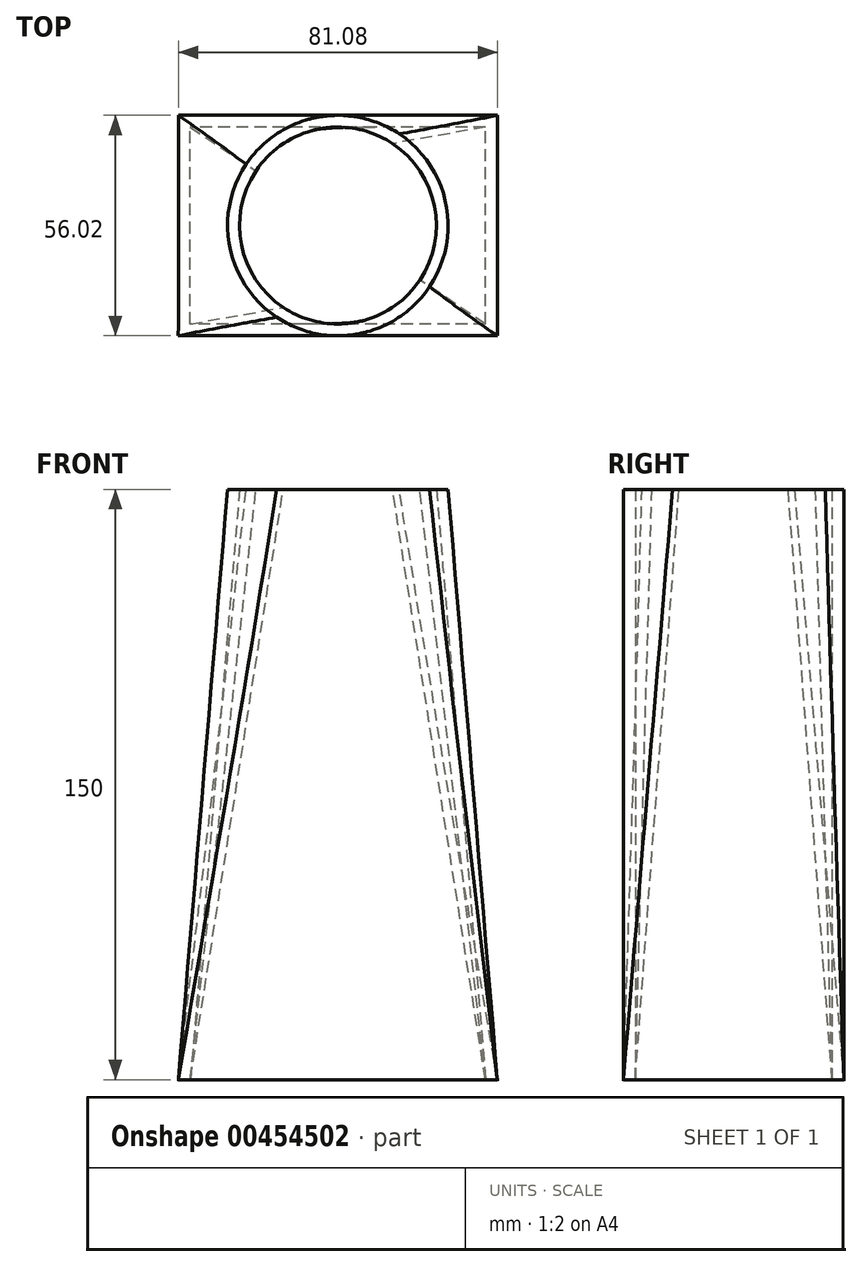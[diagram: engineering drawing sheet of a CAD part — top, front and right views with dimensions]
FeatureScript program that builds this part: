
annotation { "Feature Type Name" : "Feature", "Feature Type Description" : "" }
export const myFeature = defineFeature(function(context is Context, id is Id, definition is map)
    precondition{}
    {
        {
            var Q0;
            Q0=qCreatedBy(makeId("Top.planeOp"),FACE);
            var sketch = newSketch(context, id + "F0", { "sketchPlane" : qUnion([Q0])});
            skLineSegment(sketch, "E0.bottom", {"start": v(37.5, -25) * mm, "end": v(-37.5, -25) * mm});
            skLineSegment(sketch, "E0.top", {"start": v(37.5, 25) * mm, "end": v(-37.5, 25) * mm});
            skLineSegment(sketch, "E0.left", {"start": v(37.5, -25) * mm, "end": v(37.5, 25) * mm});
            skLineSegment(sketch, "E0.right", {"start": v(-37.5, -25) * mm, "end": v(-37.5, 25) * mm});
            skPoint(sketch, "E0.middle", {"position": v(0, 0) * mm});
            skSolve(sketch);
        }
        {
            var Q0;
            Q0=qCreatedBy(makeId("Top.planeOp"),FACE);
            cPlane(context, id + "F1", {"entities" : qUnion([Q0]), "cplaneType" : CPlaneType.OFFSET, "offset" : 150 * mm, "width" : 150 * mm, "height" : 150 * mm});
        }
        {
            var Q0;
            Q0=qCreatedBy(id+"F1.planeOp",FACE);
            var sketch = newSketch(context, id + "F2", { "sketchPlane" : qUnion([Q0])});
            skCircle(sketch, "E1", {"center": v(0, 0) * mm, "radius": 25 * mm});
            skSolve(sketch);
        }
        {
            var Q0;
            Q0=makeQuery(id+"F0.imprint","IMPRINT",FACE,{"disambiguationData":[TD([[makeQuery(id+"F0.imprint","IMPRINT",EDGE,{"derivedFrom":sQuery(id+"F0.wireOp",EDGE,"E0.bottom")}),-1.0]])]});
            var Q1;
            Q1=makeQuery(id+"F2.imprint","IMPRINT",FACE,{"disambiguationData":[TD([[makeQuery(id+"F2.imprint","IMPRINT",EDGE,{"derivedFrom":sQuery(id+"F2.wireOp",EDGE,"E1")}),1.0]])]});
            loft(context, id + "F3", {"sheetProfilesArray" : [{ "sheetProfileEntities" : qUnion([Q0]) }, { "sheetProfileEntities" : qUnion([Q1]) }]});
        }
        {
            var Q0;
            Q0=makeQuery(id+"F3.opLoft","CAP_FACE",FACE,{"disambiguationData":[OSD([makeQuery(id+"F2.imprint","IMPRINT",FACE,{"disambiguationData":[TD([[makeQuery(id+"F2.imprint","IMPRINT",EDGE,{"derivedFrom":sQuery(id+"F2.wireOp",EDGE,"E1")}),1.0]])]})])],"isStart":true});
            var Q1;
            Q1=makeQuery(id+"F3.opLoft","CAP_FACE",FACE,{"disambiguationData":[OSD([makeQuery(id+"F0.imprint","IMPRINT",FACE,{"disambiguationData":[TD([[makeQuery(id+"F0.imprint","IMPRINT",EDGE,{"derivedFrom":sQuery(id+"F0.wireOp",EDGE,"E0.bottom")}),-1.0]])]})])],"isStart":true});
            shell(context, id + "F4", {"entities" : qUnion([Q0, Q1]), "thickness" : 3 * mm, "oppositeDirection" : true});
        }
    });
